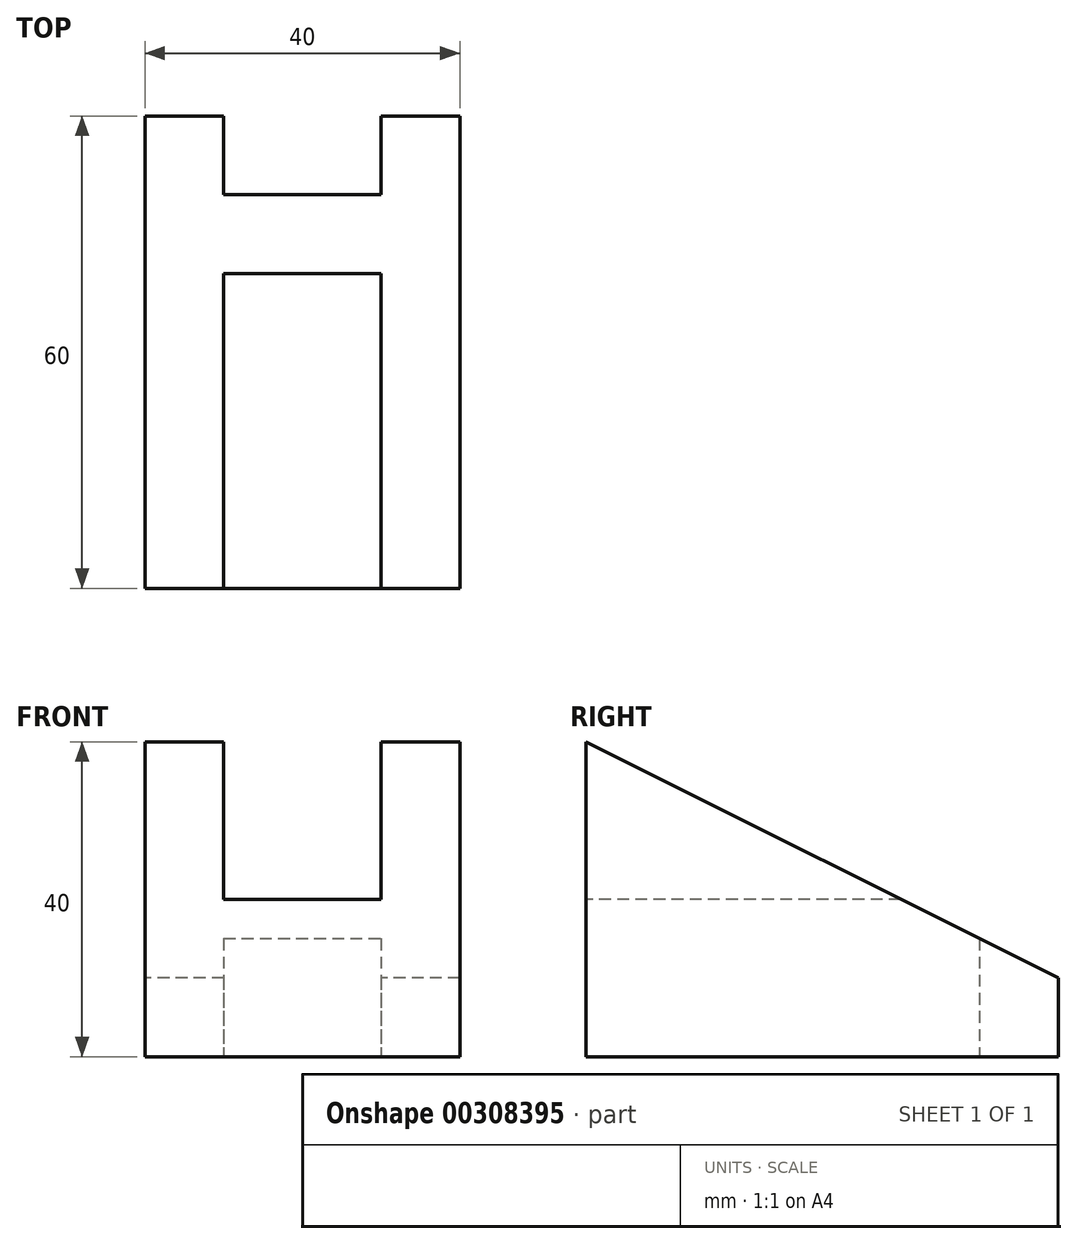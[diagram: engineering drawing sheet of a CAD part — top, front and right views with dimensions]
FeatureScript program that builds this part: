
annotation { "Feature Type Name" : "Feature", "Feature Type Description" : "" }
export const myFeature = defineFeature(function(context is Context, id is Id, definition is map)
    precondition{}
    {
        {
            var Q0;
            Q0=qCreatedBy(makeId("Right.planeOp"),FACE);
            var sketch = newSketch(context, id + "F0", { "sketchPlane" : qUnion([Q0])});
            skLineSegment(sketch, "E0", {"start": v(0, 40) * mm, "end": v(0, 0) * mm});
            skLineSegment(sketch, "E1", {"start": v(0, 0) * mm, "end": v(60, 0) * mm});
            skLineSegment(sketch, "E2", {"start": v(60, 0) * mm, "end": v(60, 10) * mm});
            skLineSegment(sketch, "E3", {"start": v(60, 10) * mm, "end": v(0, 40) * mm});
            skSolve(sketch);
        }
        {
            var Q0;
            Q0=makeQuery(id+"F0.imprint","IMPRINT",FACE,{"disambiguationData":[TD([[makeQuery(id+"F0.imprint","IMPRINT",EDGE,{"derivedFrom":sQuery(id+"F0.wireOp",EDGE,"E0")}),1.0]])]});
            extrude(context, id + "F1", {"entities" : qUnion([Q0]), "depth" : 40 * mm});
        }
        {
            var Q0;
            Q0=makeQuery(id+"F1.opExtrude","SWEPT_FACE",FACE,{"disambiguationData":[OSD([sQuery(id+"F0.wireOp",EDGE,"E1")])]});
            var sketch = newSketch(context, id + "F2", { "sketchPlane" : qUnion([Q0])});
            skLineSegment(sketch, "E4.bottom", {"start": v(10, -50) * mm, "end": v(30, -50) * mm});
            skLineSegment(sketch, "E4.top", {"start": v(10, -60) * mm, "end": v(30, -60) * mm});
            skLineSegment(sketch, "E4.left", {"start": v(10, -50) * mm, "end": v(10, -60) * mm});
            skLineSegment(sketch, "E4.right", {"start": v(30, -50) * mm, "end": v(30, -60) * mm});
            skSolve(sketch);
        }
        {
            var Q0;
            Q0=makeQuery(id+"F2.imprint","IMPRINT",FACE,{"disambiguationData":[TD([[makeQuery(id+"F2.imprint","IMPRINT",EDGE,{"derivedFrom":sQuery(id+"F2.wireOp",EDGE,"E4.bottom")}),-1.0]])]});
            extrude(context, id + "F3", {"entities" : qUnion([Q0]), "operationType" : NewBodyOperationType.REMOVE, "endBound" : BoundingType.THROUGH_ALL, "oppositeDirection" : true, "depth" : 25 * mm});
        }
        {
            var Q0;
            Q0=makeQuery(id+"F1.opExtrude","SWEPT_FACE",FACE,{"disambiguationData":[OSD([sQuery(id+"F0.wireOp",EDGE,"E0")])]});
            var sketch = newSketch(context, id + "F4", { "sketchPlane" : qUnion([Q0])});
            skLineSegment(sketch, "E5.bottom", {"start": v(10, 40) * mm, "end": v(30, 40) * mm});
            skLineSegment(sketch, "E5.top", {"start": v(10, 20) * mm, "end": v(30, 20) * mm});
            skLineSegment(sketch, "E5.left", {"start": v(10, 40) * mm, "end": v(10, 20) * mm});
            skLineSegment(sketch, "E5.right", {"start": v(30, 40) * mm, "end": v(30, 20) * mm});
            skSolve(sketch);
        }
        {
            var Q0;
            Q0 = qSketchRegion(id + "F4", true);
            extrude(context, id + "F5", {"entities" : qUnion([Q0]), "operationType" : NewBodyOperationType.REMOVE, "endBound" : BoundingType.THROUGH_ALL, "oppositeDirection" : true, "depth" : 25 * mm});
        }
    });
